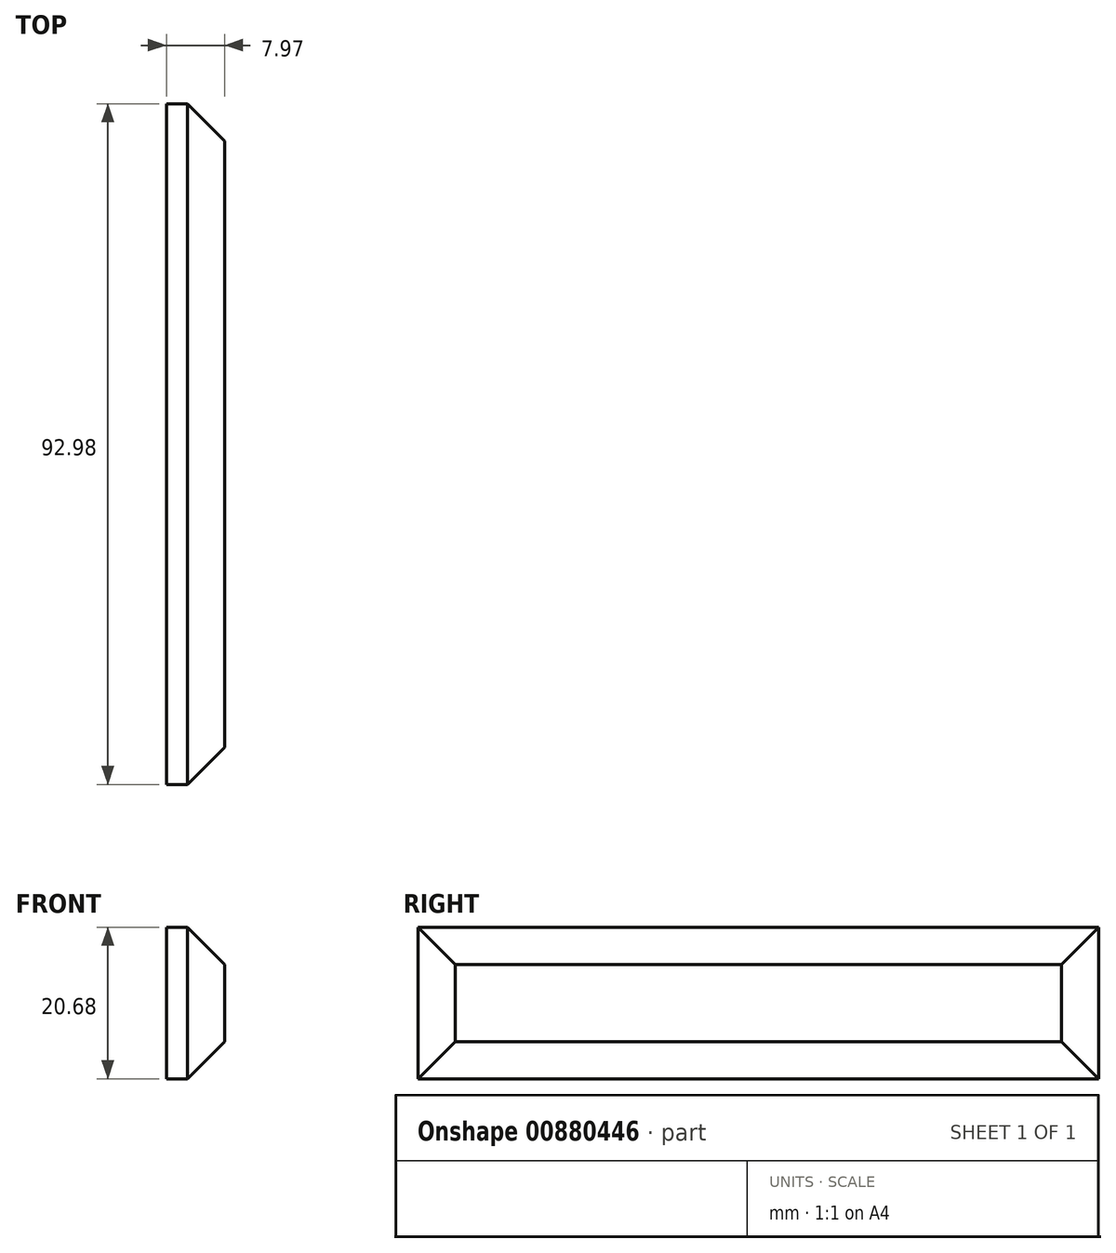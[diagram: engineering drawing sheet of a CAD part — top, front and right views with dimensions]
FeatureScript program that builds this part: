
annotation { "Feature Type Name" : "Feature", "Feature Type Description" : "" }
export const myFeature = defineFeature(function(context is Context, id is Id, definition is map)
    precondition{}
    {
        {
            var Q0;
            Q0=qCreatedBy(makeId("Top.planeOp"),FACE);
            var sketch = newSketch(context, id + "F0", { "sketchPlane" : qUnion([Q0])});
            skLineSegment(sketch, "E0.bottom", {"start": v(53.27, 60.7) * mm, "end": v(45.3, 60.7) * mm});
            skLineSegment(sketch, "E0.top", {"start": v(53.27, -32.28) * mm, "end": v(45.3, -32.28) * mm});
            skLineSegment(sketch, "E0.left", {"start": v(53.27, 60.7) * mm, "end": v(53.27, -32.28) * mm});
            skLineSegment(sketch, "E0.right", {"start": v(45.3, 60.7) * mm, "end": v(45.3, -32.28) * mm});
            skLineSegment(sketch, "E1.bottom", {"start": v(158.73, 10.05) * mm, "end": v(114.65, 10.05) * mm});
            skLineSegment(sketch, "E1.top", {"start": v(158.73, 13.39) * mm, "end": v(114.65, 13.39) * mm});
            skLineSegment(sketch, "E1.left", {"start": v(158.73, 10.05) * mm, "end": v(158.73, 13.39) * mm});
            skLineSegment(sketch, "E1.right", {"start": v(114.65, 10.05) * mm, "end": v(114.65, 13.39) * mm});
            skSolve(sketch);
        }
        {
            var Q0;
            Q0=makeQuery(id+"F0.imprint","IMPRINT",FACE,{"disambiguationData":[TD([[makeQuery(id+"F0.imprint","IMPRINT",EDGE,{"derivedFrom":sQuery(id+"F0.wireOp",EDGE,"E0.bottom")}),1.0]])]});
            extrude(context, id + "F1", {"entities" : qUnion([Q0]), "endBound" : BoundingType.SYMMETRIC, "depth" : 20.67 * mm, "offsetDistance" : 25.4 * mm});
        }
        {
            var Q0;
            Q0=makeQuery(id+"F1.opExtrude","SWEPT_FACE",FACE,{"disambiguationData":[OSD([sQuery(id+"F0.wireOp",EDGE,"E0.left")])]});
            chamfer(context, id + "F2", {"entities" : qUnion([Q0]), "width" : 5.08 * mm, "tangentPropagation" : true});
        }
    });
